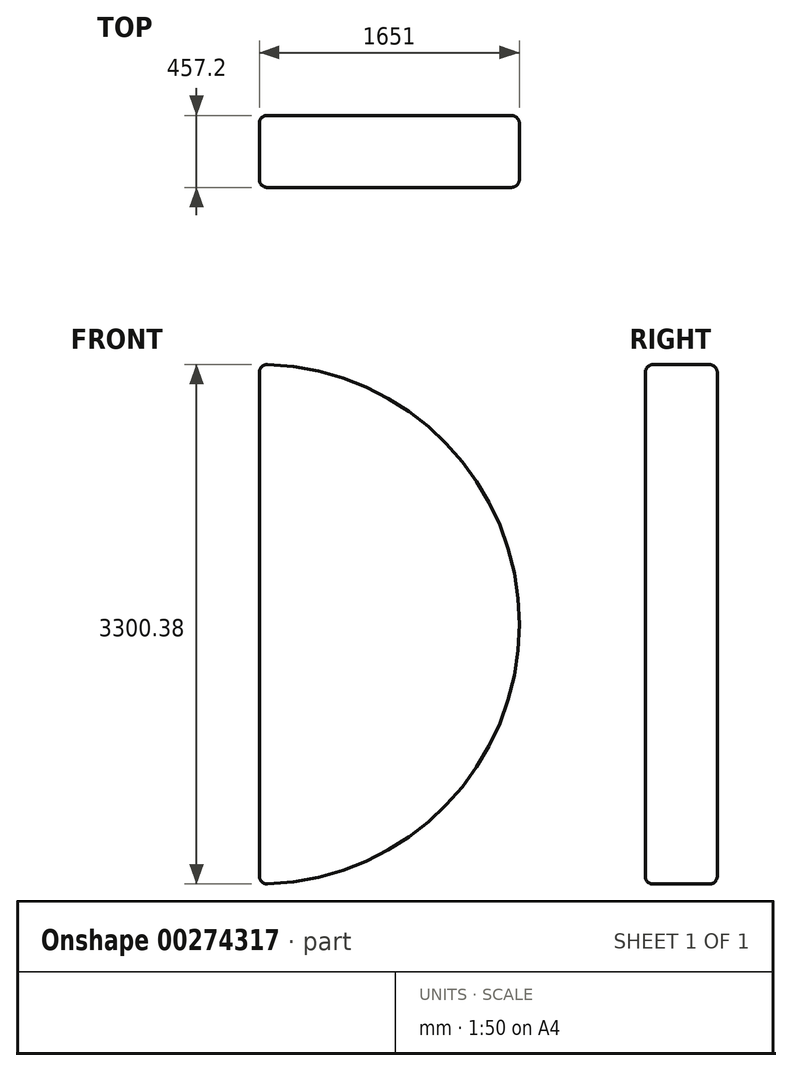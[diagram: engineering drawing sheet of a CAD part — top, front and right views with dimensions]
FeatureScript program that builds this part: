
annotation { "Feature Type Name" : "Feature", "Feature Type Description" : "" }
export const myFeature = defineFeature(function(context is Context, id is Id, definition is map)
    precondition{}
    {
        {
            var Q0;
            Q0=qCreatedBy(makeId("Front.planeOp"),FACE);
            var sketch = newSketch(context, id + "F0", { "sketchPlane" : qUnion([Q0])});
            skLineSegment(sketch, "E0", {"start": v(0, 0) * mm, "end": v(0, 1651) * mm});
            skArc(sketch, "E1", {"start": v(0, 1651) * mm, "mid": v(1167.43, 1167.43) * mm, "end": v(1651, 0) * mm});
            skArc(sketch, "E2", {"start": v(1651, 0) * mm, "mid": v(1167.43, -1167.43) * mm, "end": v(0, -1651) * mm});
            skLineSegment(sketch, "E3", {"start": v(0, 0) * mm, "end": v(0, -1651) * mm});
            skSolve(sketch);
        }
        {
            var Q0;
            Q0=makeQuery(id+"F0.imprint","IMPRINT",FACE,{"disambiguationData":[TD([[makeQuery(id+"F0.imprint","IMPRINT",EDGE,{"derivedFrom":sQuery(id+"F0.wireOp",EDGE,"E0")}),-1.0]])]});
            extrude(context, id + "F1", {"entities" : qUnion([Q0]), "oppositeDirection" : true, "depth" : 457.2 * mm});
        }
        {
            var Q0;
            Q0=makeQuery(id+"F1.opExtrude","SWEPT_EDGE",EDGE,{"disambiguationData":[OSD([sQuery(id+"F0.wireOp",EDGE,"E0"),sQuery(id+"F0.wireOp",EDGE,"E1")])]});
            var Q1;
            Q1=makeQuery(id+"F1.opExtrude","CAP_EDGE",EDGE,{"disambiguationData":[OSD([sQuery(id+"F0.wireOp",EDGE,"E1"),sQuery(id+"F0.wireOp",EDGE,"E2")])],"isStart":false});
            var Q2;
            Q2=makeQuery(id+"F1.opExtrude","CAP_EDGE",EDGE,{"disambiguationData":[OSD([sQuery(id+"F0.wireOp",EDGE,"E1"),sQuery(id+"F0.wireOp",EDGE,"E2")])],"isStart":true});
            var Q3;
            Q3=makeQuery(id+"F1.opExtrude","SWEPT_EDGE",EDGE,{"disambiguationData":[OSD([sQuery(id+"F0.wireOp",EDGE,"E2"),sQuery(id+"F0.wireOp",EDGE,"E3")])]});
            var Q4;
            Q4=makeQuery(id+"F1.opExtrude","CAP_EDGE",EDGE,{"disambiguationData":[OSD([sQuery(id+"F0.wireOp",EDGE,"E0"),sQuery(id+"F0.wireOp",EDGE,"E3")])],"isStart":true});
            var Q5;
            Q5=makeQuery(id+"F1.opExtrude","CAP_EDGE",EDGE,{"disambiguationData":[OSD([sQuery(id+"F0.wireOp",EDGE,"E0"),sQuery(id+"F0.wireOp",EDGE,"E3")])],"isStart":false});
            fillet(context, id + "F2", {"entities" : qUnion([Q0, Q1, Q2, Q3, Q4, Q5]), "radius" : 50.8 * mm, "tangentPropagation" : true, "allowEdgeOverflow" : false});
        }
    });
